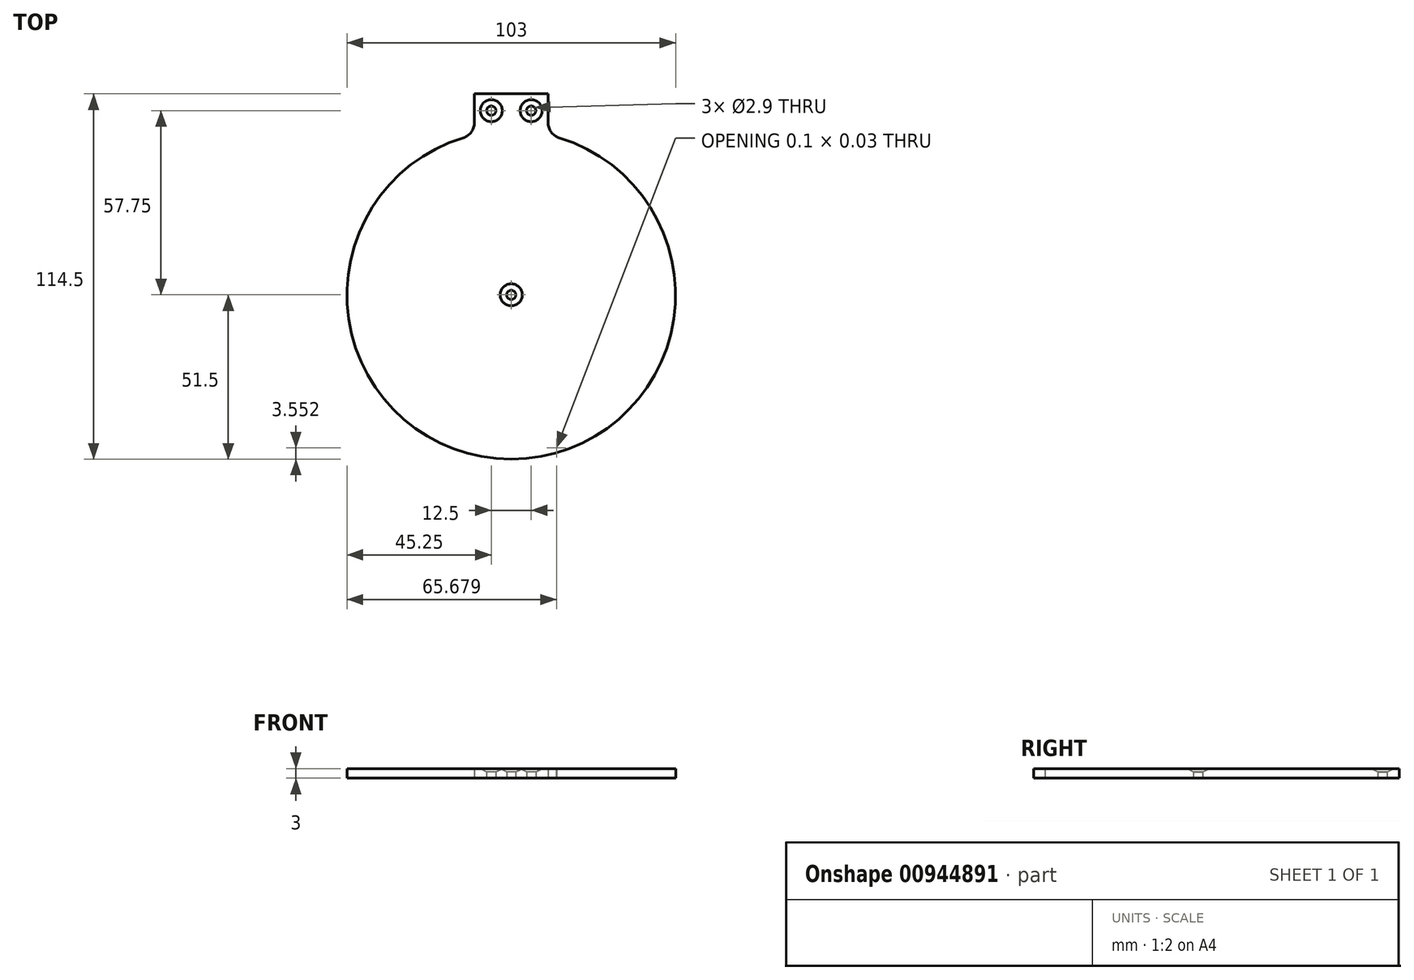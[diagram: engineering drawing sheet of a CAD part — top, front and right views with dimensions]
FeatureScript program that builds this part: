
annotation { "Feature Type Name" : "Feature", "Feature Type Description" : "" }
export const myFeature = defineFeature(function(context is Context, id is Id, definition is map)
    precondition{}
    {
        {
            var Q0;
            Q0=qCreatedBy(makeId("Top.planeOp"),FACE);
            var sketch = newSketch(context, id + "F0", { "sketchPlane" : qUnion([Q0])});
            skArc(sketch, "E0", {"start": v(-15.04, 49.25) * mm, "mid": v(0, -51.5) * mm, "end": v(15.04, 49.25) * mm});
            skCircle(sketch, "E1", {"center": v(0, 0) * mm, "radius": 10 * mm, "construction": true});
            skCircle(sketch, "E2", {"center": v(0, 0) * mm, "radius": 11.5 * mm, "construction": true});
            skLineSegment(sketch, "E3", {"start": v(11.5, 54.04) * mm, "end": v(11.5, 63) * mm});
            skLineSegment(sketch, "E4", {"start": v(11.5, 63) * mm, "end": v(-11.5, 63) * mm});
            skLineSegment(sketch, "E5.trimOffspring", {"start": v(-11.5, 54.04) * mm, "end": v(-11.5, 63) * mm});
            skPoint(sketch, "E6.start.orphan", {"position": v(-11.5, 0) * mm});
            skPoint(sketch, "E7.orphan", {"position": v(11.5, 0) * mm});
            skPoint(sketch, "E8.visualSharp", {"position": v(-10, 48.99) * mm});
            skPoint(sketch, "E9.visualSharp", {"position": v(10, 48.99) * mm});
            skArc(sketch, "E9.filletArc", {"start": v(14.23, -47.93) * mm, "mid": v(14.18, -47.95) * mm, "end": v(14.13, -47.96) * mm});
            skPoint(sketch, "E10.visualSharp", {"position": v(11.5, 50.2) * mm});
            skArc(sketch, "E11", {"start": v(14.13, -47.96) * mm, "mid": v(14.18, -47.95) * mm, "end": v(14.23, -47.93) * mm});
            skLineSegment(sketch, "E12", {"start": v(15.04, 49.25) * mm, "end": v(15.04, 49.25) * mm});
            skLineSegment(sketch, "E13", {"start": v(-11.5, 54.04) * mm, "end": v(-11.5, 54.04) * mm});
            skLineSegment(sketch, "E14", {"start": v(11.5, 54.04) * mm, "end": v(11.5, 54.04) * mm});
            skLineSegment(sketch, "E15.trimOffspring", {"start": v(-15.04, 49.25) * mm, "end": v(-15.04, 49.25) * mm});
            skPoint(sketch, "E16.start.orphan", {"position": v(10, 0) * mm});
            skPoint(sketch, "E17.start.orphan", {"position": v(-10, 0) * mm});
            skPoint(sketch, "E18.visualSharp", {"position": v(-11.5, 50.2) * mm});
            skArc(sketch, "E18.filletArc", {"start": v(-15.04, 49.25) * mm, "mid": v(-12.48, 51.06) * mm, "end": v(-11.5, 54.04) * mm});
            skArc(sketch, "E19.filletArc", {"start": v(11.5, 54.04) * mm, "mid": v(12.48, 51.06) * mm, "end": v(15.04, 49.25) * mm});
            skPoint(sketch, "E20.visualSharp", {"position": v(10, 49.23) * mm});
            skPoint(sketch, "E21.visualSharp", {"position": v(-10, 49.1) * mm});
            skLineSegment(sketch, "E22.direction1", {"start": v(-6.25, 57.75) * mm, "end": v(0, 57.75) * mm, "construction": true});
            skCircle(sketch, "E23", {"center": v(0, 0) * mm, "radius": 1.45 * mm});
            skLineSegment(sketch, "E24", {"start": v(0, 0) * mm, "end": v(0, 57.75) * mm, "construction": true});
            skCircle(sketch, "E25", {"center": v(-6.25, 57.75) * mm, "radius": 1.45 * mm});
            skCircle(sketch, "E26", {"center": v(6.25, 57.75) * mm, "radius": 1.45 * mm});
            skSolve(sketch);
        }
        {
            var Q0;
            Q0 = qSketchRegion(id + "F0", true);
            extrude(context, id + "F1", {"entities" : qUnion([Q0]), "depth" : 3 * mm, "offsetDistance" : 25 * mm});
        }
        {
            var Q0;
            Q0=makeQuery(id+"F1.opExtrude","CAP_EDGE",EDGE,{"disambiguationData":[OSD([sQuery(id+"F0.wireOp",EDGE,"E25")])],"isStart":false});
            var Q1;
            Q1=makeQuery(id+"F1.opExtrude","CAP_EDGE",EDGE,{"disambiguationData":[OSD([sQuery(id+"F0.wireOp",EDGE,"E26")])],"isStart":false});
            var Q2;
            Q2=makeQuery(id+"F1.opExtrude","CAP_EDGE",EDGE,{"disambiguationData":[OSD([sQuery(id+"F0.wireOp",EDGE,"E23")])],"isStart":false});
            chamfer(context, id + "F2", {"entities" : qUnion([Q0, Q1, Q2]), "chamferType" : ChamferType.TWO_OFFSETS, "width1" : 1 * mm, "oppositeDirection" : false, "width2" : 2 * mm, "tangentPropagation" : true});
        }
    });
